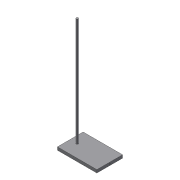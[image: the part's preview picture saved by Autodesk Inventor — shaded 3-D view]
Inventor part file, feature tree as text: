
AUTODESK INVENTOR PART (.ipt)
format: ipt  version: 2017 (Build 210142000, 142)  size: 93,696 bytes
history: native  units: in
note: dims shown in document units (in); Inventor stores cm internally (conversion verified against a paired STEP export)
features: extrude x3, sketch x3, projected_geometry x2
ambient origin geometry x8: Origin, YZ Plane, XZ Plane, XY Plane, X Axis, Y Axis, Z Axis, Center Point
bodies: Solid1 (feature_tree)
feature tree (8):
  extrude  "Extrusion1"  Depth=8.375in
  extrude  "Extrusion2"  Depth=0.6299in
  extrude  "Extrusion3"  Depth=23.0in TaperAngle=0.0deg
  sketch  "Sketch1"  dims[d0=5.4614in d1=8.375in]
  sketch  "Sketch2"  dims[d2=0.6299in d3=0.0in d4=0.4638in]
  projected_geometry  "Projected Loop1"
  sketch  "Sketch3"  dims[d5=1.2402in d6=23.0in d7=0.0in d8=0.2756in d9=0.0098in d10=0.0in]
  projected_geometry  "Projected Loop2"
